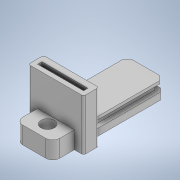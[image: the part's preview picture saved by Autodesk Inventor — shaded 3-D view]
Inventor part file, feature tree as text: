
AUTODESK INVENTOR PART (.ipt)
format: ipt  version: 2021.1 (Build 251245010, 245A)  size: 237,568 bytes
history: native  units: mm
features: move_body x7, extrude x1, direct_edit x1, fillet x1, sketch x1, other x1
ambient origin geometry x8: Origin, YZ Plane, XZ Plane, XY Plane, X Axis, Y Axis, Z Axis, Center Point
bodies: Volumenkörper1 (feature_tree)
feature tree (12):
  extrude  "Extrusion1"  TaperAngle=0.0deg  [1 undecoded]
  direct_edit  "Direktbearbeitung1"
  fillet  "Rundung1"  [1 undecoded]
  sketch  "Skizze1"  dims[d0=25.0mm d1=0.0mm d2=0.0mm d3=0.0mm d4=-3.0mm d5=0.0mm d6=-21.65mm d7=0.0mm d8=0.0mm d9=-3.25mm d10=0.0mm d11=0.0mm d12=0.0mm d13=-9.0mm d14=0.0mm d15=0.0mm d16=-1.5mm d20=3.0mm d21=0.0mm d22=0.0mm d23=0.5mm d24=0.0mm d25=0.0mm d26=1.0mm]
  other  "Körper24"
  move_body  "Verschieben1"
  move_body  "Verschieben2"
  move_body  "Verschieben3"
  move_body  "Verschieben4"
  move_body  "Verschieben5"
  move_body  "Verschieben6"
  move_body  "Verschieben7"
note: 2 required parameter values undecoded (feature->parameter linkage not recoverable at this tier; creation-order binding heuristic only, values carry confidence <= 0.55)
